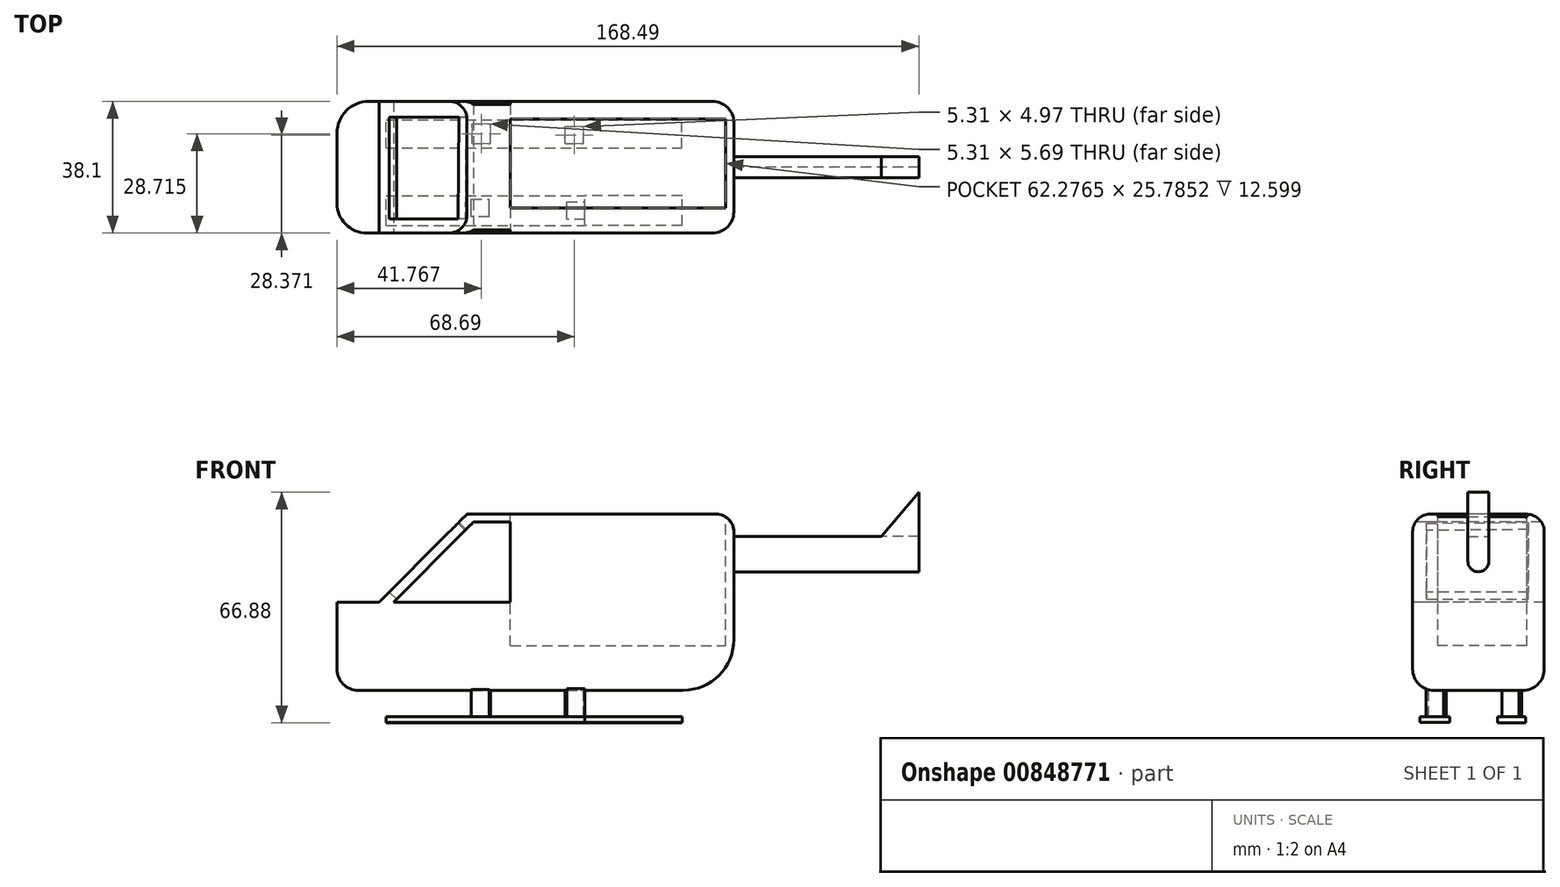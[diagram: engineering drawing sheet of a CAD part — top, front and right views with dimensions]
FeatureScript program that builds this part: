
annotation { "Feature Type Name" : "Feature", "Feature Type Description" : "" }
export const myFeature = defineFeature(function(context is Context, id is Id, definition is map)
    precondition{}
    {
        {
            var Q0;
            Q0=qCreatedBy(makeId("Front.planeOp"),FACE);
            var sketch = newSketch(context, id + "F0", { "sketchPlane" : qUnion([Q0])});
            skLineSegment(sketch, "E0.bottom", {"start": v(-38.01, 25.5) * mm, "end": v(38.01, 25.5) * mm});
            skLineSegment(sketch, "E0.top", {"start": v(-38.01, -25.5) * mm, "end": v(38.01, -25.5) * mm});
            skLineSegment(sketch, "E0.left", {"start": v(-38.01, 25.5) * mm, "end": v(-38.01, -25.5) * mm});
            skLineSegment(sketch, "E0.right", {"start": v(38.01, 25.5) * mm, "end": v(38.01, -25.5) * mm});
            skPoint(sketch, "E0.middle", {"position": v(0, 0) * mm});
            skSolve(sketch);
        }
        {
            var Q0;
            Q0=makeQuery(id+"F0.imprint","IMPRINT",FACE,{"disambiguationData":[TD([[makeQuery(id+"F0.imprint","IMPRINT",EDGE,{"derivedFrom":sQuery(id+"F0.wireOp",EDGE,"E0.bottom")}),-1.0]])]});
            extrude(context, id + "F1", {"entities" : qUnion([Q0]), "depth" : 38.1 * mm, "offsetDistance" : 25.4 * mm});
        }
        {
            var Q0;
            Q0=makeQuery(id+"F1.opExtrude","CAP_FACE",FACE,{"disambiguationData":[OSD([sQuery(id+"F0.wireOp",EDGE,"E0.bottom"),sQuery(id+"F0.wireOp",EDGE,"E0.top"),sQuery(id+"F0.wireOp",EDGE,"E0.left"),sQuery(id+"F0.wireOp",EDGE,"E0.right")])],"isStart":false});
            var sketch = newSketch(context, id + "F2", { "sketchPlane" : qUnion([Q0])});
            skLineSegment(sketch, "E1", {"start": v(-38.01, 0) * mm, "end": v(-12.6, 25.5) * mm});
            skLineSegment(sketch, "E2", {"start": v(-12.6, 25.5) * mm, "end": v(-38.01, 25.5) * mm});
            skLineSegment(sketch, "E3", {"start": v(-38.01, 25.5) * mm, "end": v(-38.01, 0) * mm});
            skSolve(sketch);
        }
        {
            var Q0;
            Q0=makeQuery(id+"F2.imprint","IMPRINT",FACE,{"disambiguationData":[TD([[makeQuery(id+"F2.imprint","IMPRINT",EDGE,{"derivedFrom":sQuery(id+"F2.wireOp",EDGE,"E1")}),1.0]])]});
            extrude(context, id + "F3", {"entities" : qUnion([Q0]), "operationType" : NewBodyOperationType.REMOVE, "oppositeDirection" : true, "depth" : 38.1 * mm, "offsetDistance" : 25.4 * mm});
        }
        {
            var Q0;
            Q0=makeQuery(id+"F1.opExtrude","CAP_FACE",FACE,{"disambiguationData":[OSD([sQuery(id+"F0.wireOp",EDGE,"E0.bottom"),sQuery(id+"F0.wireOp",EDGE,"E0.top"),sQuery(id+"F0.wireOp",EDGE,"E0.left"),sQuery(id+"F0.wireOp",EDGE,"E0.right")])],"isStart":false});
            var sketch = newSketch(context, id + "F4", { "sketchPlane" : qUnion([Q0])});
            skLineSegment(sketch, "E4", {"start": v(-33.84, 0) * mm, "end": v(-10.7, 23.22) * mm});
            skLineSegment(sketch, "E5", {"start": v(-10.7, 23.22) * mm, "end": v(0, 23.22) * mm});
            skLineSegment(sketch, "E6", {"start": v(0, 23.22) * mm, "end": v(0, 0) * mm});
            skLineSegment(sketch, "E7", {"start": v(0, 0) * mm, "end": v(-33.84, 0) * mm});
            skSolve(sketch);
        }
        {
            var Q0;
            Q0=makeQuery(id+"F4.imprint","IMPRINT",FACE,{"disambiguationData":[TD([[makeQuery(id+"F4.imprint","IMPRINT",EDGE,{"derivedFrom":sQuery(id+"F4.wireOp",EDGE,"E4")}),-1.0]])]});
            extrude(context, id + "F5", {"entities" : qUnion([Q0]), "operationType" : NewBodyOperationType.REMOVE, "oppositeDirection" : true, "depth" : 38.1 * mm, "offsetDistance" : 25.4 * mm});
        }
        {
            var Q0;
            Q0=makeQuery(id+"F3.boolean.opBoolean","COPY",FACE,{"derivedFrom":makeQuery(id+"F3.opExtrude","SWEPT_FACE",FACE,{"disambiguationData":[OSD([sQuery(id+"F2.wireOp",EDGE,"E1")])]})});
            var sketch = newSketch(context, id + "F6", { "sketchPlane" : qUnion([Q0])});
            skLineSegment(sketch, "E8", {"start": v(4.6, 5.84) * mm, "end": v(4.6, -22.68) * mm});
            skLineSegment(sketch, "E9", {"start": v(4.6, -22.68) * mm, "end": v(34.03, -22.68) * mm});
            skLineSegment(sketch, "E10", {"start": v(34.03, -22.68) * mm, "end": v(34.03, 5.47) * mm});
            skLineSegment(sketch, "E11", {"start": v(34.03, 5.47) * mm, "end": v(4.6, 5.84) * mm});
            skSolve(sketch);
        }
        {
            var Q0;
            Q0=makeQuery(id+"F6.imprint","IMPRINT",FACE,{"disambiguationData":[TD([[makeQuery(id+"F6.imprint","IMPRINT",EDGE,{"derivedFrom":sQuery(id+"F6.wireOp",EDGE,"E8")}),1.0]])]});
            extrude(context, id + "F7", {"entities" : qUnion([Q0]), "operationType" : NewBodyOperationType.REMOVE, "oppositeDirection" : true, "depth" : 3.8 * mm, "offsetDistance" : 25.4 * mm});
        }
        {
            var Q0;
            Q0=makeQuery(id+"F1.opExtrude","SWEPT_FACE",FACE,{"disambiguationData":[OSD([sQuery(id+"F0.wireOp",EDGE,"E0.right")])]});
            var sketch = newSketch(context, id + "F8", { "sketchPlane" : qUnion([Q0])});
            skLineSegment(sketch, "E12.bottom", {"start": v(-22.1, 19.05) * mm, "end": v(-16.02, 19.05) * mm});
            skLineSegment(sketch, "E12.top", {"start": v(-22.1, 8.82) * mm, "end": v(-16.02, 8.82) * mm});
            skLineSegment(sketch, "E12.left", {"start": v(-22.1, 19.05) * mm, "end": v(-22.1, 8.82) * mm});
            skLineSegment(sketch, "E12.right", {"start": v(-16.02, 19.05) * mm, "end": v(-16.02, 8.82) * mm});
            skSolve(sketch);
        }
        {
            var Q0;
            Q0=makeQuery(id+"F1.opExtrude","SWEPT_FACE",FACE,{"disambiguationData":[OSD([sQuery(id+"F0.wireOp",EDGE,"E0.bottom")])]});
            var sketch = newSketch(context, id + "F9", { "sketchPlane" : qUnion([Q0])});
            skSolve(sketch);
        }
        {
            var Q0;
            Q0=makeQuery(id+"F8.imprint","IMPRINT",FACE,{"disambiguationData":[TD([[makeQuery(id+"F8.imprint","IMPRINT",EDGE,{"derivedFrom":sQuery(id+"F8.wireOp",EDGE,"E12.bottom")}),1.0]])]});
            extrude(context, id + "F10", {"entities" : qUnion([Q0]), "operationType" : NewBodyOperationType.ADD, "depth" : 26.67 * mm, "offsetDistance" : 25.4 * mm});
        }
        {
            var Q0;
            Q0 = qSketchRegion(id + "F8", true);
            extrude(context, id + "F11", {"entities" : qUnion([Q0]), "operationType" : NewBodyOperationType.ADD, "depth" : 80.26 * mm, "offsetDistance" : 25.4 * mm});
        }
        {
            var Q0;
            Q0=makeQuery(id+"F11.opExtrude","SWEPT_FACE",FACE,{"disambiguationData":[OSD([sQuery(id+"F8.wireOp",EDGE,"E12.left")])]});
            var sketch = newSketch(context, id + "F12", { "sketchPlane" : qUnion([Q0])});
            skLineSegment(sketch, "E13", {"start": v(118.28, 19.05) * mm, "end": v(118.28, 31.95) * mm});
            skLineSegment(sketch, "E14", {"start": v(118.28, 31.95) * mm, "end": v(107.4, 19.05) * mm});
            skLineSegment(sketch, "E15", {"start": v(107.4, 19.05) * mm, "end": v(118.28, 19.05) * mm});
            skSolve(sketch);
        }
        {
            var Q0;
            Q0=makeQuery(id+"F12.imprint","IMPRINT",FACE,{"disambiguationData":[TD([[makeQuery(id+"F12.imprint","IMPRINT",EDGE,{"derivedFrom":sQuery(id+"F12.wireOp",EDGE,"E13")}),1.0]])]});
            extrude(context, id + "F13", {"entities" : qUnion([Q0]), "operationType" : NewBodyOperationType.ADD, "oppositeDirection" : true, "depth" : 6.1 * mm, "offsetDistance" : 25.4 * mm});
        }
        {
            var Q0;
            {var subQ0=sQuery(id+"F0.wireOp",EDGE,"E0.bottom");Q0=makeQuery(id+"F9.imprint","IMPRINT",FACE,{"disambiguationData":[TD([[makeQuery(id+"F9.imprint","IMPRINT",EDGE,{"derivedFrom":makeQuery(id+"F1.opExtrude","CAP_EDGE",EDGE,{"disambiguationData":[OSD([subQ0])],"isStart":true})}),-1.0]])]});}
            var sketch = newSketch(context, id + "F14", { "sketchPlane" : qUnion([Q0])});
            skLineSegment(sketch, "E16.bottom", {"start": v(0, -5.02) * mm, "end": v(62.28, -5.02) * mm});
            skLineSegment(sketch, "E16.top", {"start": v(0, -30.8) * mm, "end": v(62.28, -30.8) * mm});
            skLineSegment(sketch, "E16.left", {"start": v(0, -5.02) * mm, "end": v(0, -30.8) * mm});
            skLineSegment(sketch, "E16.right", {"start": v(62.28, -5.02) * mm, "end": v(62.28, -30.8) * mm});
            skSolve(sketch);
        }
        {
            var Q0;
            {var subQ0=sQuery(id+"F14.wireOp",EDGE,"E16.left");Q0=makeQuery(id+"F14.imprint","IMPRINT",FACE,{"disambiguationData":[TD([[makeQuery(id+"F14.imprint","IMPRINT",EDGE,{"derivedFrom":subQ0}),1.0]])]});}
            var Q1;
            {var subQ0=sQuery(id+"F14.wireOp",EDGE,"E16.right");Q1=makeQuery(id+"F14.imprint","IMPRINT",FACE,{"disambiguationData":[TD([[makeQuery(id+"F14.imprint","IMPRINT",EDGE,{"derivedFrom":subQ0}),-1.0]])]});}
            extrude(context, id + "F15", {"entities" : qUnion([Q0, Q1]), "operationType" : NewBodyOperationType.REMOVE, "oppositeDirection" : true, "depth" : 38.1 * mm, "offsetDistance" : 25.4 * mm});
        }
        {
            var Q0;
            Q0=makeQuery(id+"F1.opExtrude","SWEPT_FACE",FACE,{"disambiguationData":[OSD([sQuery(id+"F0.wireOp",EDGE,"E0.left")])]});
            extrude(context, id + "F16", {"entities" : qUnion([Q0]), "operationType" : NewBodyOperationType.ADD, "depth" : 12.2 * mm, "offsetDistance" : 25.4 * mm});
        }
        {
            var Q0;
            {var subQ0=sQuery(id+"F0.wireOp",EDGE,"E0.top");Q0=makeQuery(id+"F16.boolean.opBoolean","MERGE",FACE,{"derivedFrom":[makeQuery(id+"F10.boolean.opBoolean","MERGE",FACE,{"derivedFrom":[makeQuery(id+"F1.opExtrude","SWEPT_FACE",FACE,{"disambiguationData":[OSD([subQ0])]}),makeQuery(id+"F10.opExtrude","SWEPT_FACE",FACE,{"disambiguationData":[OSD([subQ0,sQuery(id+"F0.wireOp",EDGE,"E0.right")])]})]}),makeQuery(id+"F16.opExtrude","SWEPT_FACE",FACE,{"disambiguationData":[OSD([subQ0,sQuery(id+"F0.wireOp",EDGE,"E0.left")])]})]});}
            var sketch = newSketch(context, id + "F17", { "sketchPlane" : qUnion([Q0])});
            skLineSegment(sketch, "E17.bottom", {"start": v(-11.29, 33.46) * mm, "end": v(-6.17, 33.46) * mm});
            skLineSegment(sketch, "E17.top", {"start": v(-11.29, 28.34) * mm, "end": v(-6.17, 28.34) * mm});
            skLineSegment(sketch, "E17.left", {"start": v(-11.29, 33.46) * mm, "end": v(-11.29, 28.34) * mm});
            skLineSegment(sketch, "E17.right", {"start": v(-6.17, 33.46) * mm, "end": v(-6.17, 28.34) * mm});
            skSolve(sketch);
        }
        {
            var Q0;
            Q0=makeQuery(id+"F17.imprint","IMPRINT",FACE,{"disambiguationData":[TD([[makeQuery(id+"F17.imprint","IMPRINT",EDGE,{"derivedFrom":sQuery(id+"F17.wireOp",EDGE,"E17.bottom")}),1.0]])]});
            var sketch = newSketch(context, id + "F18", { "sketchPlane" : qUnion([Q0])});
            skLineSegment(sketch, "E18.bottom", {"start": v(-11.1, 12.23) * mm, "end": v(-5.79, 12.23) * mm});
            skLineSegment(sketch, "E18.top", {"start": v(-11.1, 6.54) * mm, "end": v(-5.79, 6.54) * mm});
            skLineSegment(sketch, "E18.left", {"start": v(-11.1, 12.23) * mm, "end": v(-11.1, 6.54) * mm});
            skLineSegment(sketch, "E18.right", {"start": v(-5.79, 12.23) * mm, "end": v(-5.79, 6.54) * mm});
            skSolve(sketch);
        }
        {
            var Q0;
            Q0=makeQuery(id+"F17.imprint","IMPRINT",FACE,{"disambiguationData":[TD([[makeQuery(id+"F17.imprint","IMPRINT",EDGE,{"derivedFrom":sQuery(id+"F17.wireOp",EDGE,"E17.bottom")}),1.0]])]});
            var sketch = newSketch(context, id + "F19", { "sketchPlane" : qUnion([Q0])});
            skLineSegment(sketch, "E19.bottom", {"start": v(16.4, 34.22) * mm, "end": v(21.51, 34.22) * mm});
            skLineSegment(sketch, "E19.top", {"start": v(16.4, 29.1) * mm, "end": v(21.51, 29.1) * mm});
            skLineSegment(sketch, "E19.left", {"start": v(16.4, 34.22) * mm, "end": v(16.4, 29.1) * mm});
            skLineSegment(sketch, "E19.right", {"start": v(21.51, 34.22) * mm, "end": v(21.51, 29.1) * mm});
            skSolve(sketch);
        }
        {
            var Q0;
            Q0=makeQuery(id+"F17.imprint","IMPRINT",FACE,{"disambiguationData":[TD([[makeQuery(id+"F17.imprint","IMPRINT",EDGE,{"derivedFrom":sQuery(id+"F17.wireOp",EDGE,"E17.bottom")}),1.0]])]});
            var sketch = newSketch(context, id + "F20", { "sketchPlane" : qUnion([Q0])});
            skLineSegment(sketch, "E20.bottom", {"start": v(15.83, 12.21) * mm, "end": v(21.13, 12.21) * mm});
            skLineSegment(sketch, "E20.top", {"start": v(15.83, 7.24) * mm, "end": v(21.13, 7.24) * mm});
            skLineSegment(sketch, "E20.left", {"start": v(15.83, 12.21) * mm, "end": v(15.83, 7.24) * mm});
            skLineSegment(sketch, "E20.right", {"start": v(21.13, 12.21) * mm, "end": v(21.13, 7.24) * mm});
            skSolve(sketch);
        }
        {
            var Q0;
            Q0=makeQuery(id+"F18.imprint","IMPRINT",FACE,{"disambiguationData":[TD([[makeQuery(id+"F18.imprint","IMPRINT",EDGE,{"derivedFrom":sQuery(id+"F18.wireOp",EDGE,"E18.bottom")}),-1.0]])]});
            extrude(context, id + "F21", {"entities" : qUnion([Q0]), "operationType" : NewBodyOperationType.ADD, "depth" : 7.62 * mm, "offsetDistance" : 25.4 * mm});
        }
        {
            var Q0;
            Q0=makeQuery(id+"F17.imprint","IMPRINT",FACE,{"disambiguationData":[TD([[makeQuery(id+"F17.imprint","IMPRINT",EDGE,{"derivedFrom":sQuery(id+"F17.wireOp",EDGE,"E17.bottom")}),-1.0]])]});
            extrude(context, id + "F22", {"entities" : qUnion([Q0]), "operationType" : NewBodyOperationType.ADD, "depth" : 7.62 * mm, "offsetDistance" : 25.4 * mm});
        }
        {
            var Q0;
            Q0=makeQuery(id+"F19.imprint","IMPRINT",FACE,{"disambiguationData":[TD([[makeQuery(id+"F19.imprint","IMPRINT",EDGE,{"derivedFrom":sQuery(id+"F19.wireOp",EDGE,"E19.bottom")}),-1.0]])]});
            extrude(context, id + "F23", {"entities" : qUnion([Q0]), "operationType" : NewBodyOperationType.ADD, "depth" : 7.62 * mm, "offsetDistance" : 25.4 * mm});
        }
        {
            var Q0;
            Q0=makeQuery(id+"F20.imprint","IMPRINT",FACE,{"disambiguationData":[TD([[makeQuery(id+"F20.imprint","IMPRINT",EDGE,{"derivedFrom":sQuery(id+"F20.wireOp",EDGE,"E20.bottom")}),-1.0]])]});
            extrude(context, id + "F24", {"entities" : qUnion([Q0]), "operationType" : NewBodyOperationType.ADD, "depth" : 7.62 * mm, "offsetDistance" : 25.4 * mm});
        }
        {
            var Q0;
            Q0=makeQuery(id+"F24.opExtrude","SWEPT_FACE",FACE,{"disambiguationData":[OSD([sQuery(id+"F20.wireOp",EDGE,"E20.right")])]});
            var sketch = newSketch(context, id + "F25", { "sketchPlane" : qUnion([Q0])});
            skLineSegment(sketch, "E21.bottom", {"start": v(-13.52, -33.12) * mm, "end": v(-5.4, -33.12) * mm});
            skLineSegment(sketch, "E21.top", {"start": v(-13.52, -34.93) * mm, "end": v(-5.4, -34.93) * mm});
            skLineSegment(sketch, "E21.left", {"start": v(-13.52, -33.12) * mm, "end": v(-13.52, -34.93) * mm});
            skLineSegment(sketch, "E21.right", {"start": v(-5.4, -33.12) * mm, "end": v(-5.4, -34.93) * mm});
            skSolve(sketch);
        }
        {
            var Q0;
            Q0=makeQuery(id+"F25.imprint","IMPRINT",FACE,{"disambiguationData":[TD([[makeQuery(id+"F25.imprint","IMPRINT",EDGE,{"derivedFrom":sQuery(id+"F25.wireOp",EDGE,"E21.top")}),1.0]])]});
            extrude(context, id + "F26", {"entities" : qUnion([Q0]), "operationType" : NewBodyOperationType.ADD, "oppositeDirection" : true, "depth" : 57.15 * mm, "offsetDistance" : 25.4 * mm});
        }
        {
            var Q0;
            Q0=makeQuery(id+"F26.boolean.opBoolean","MERGE",FACE,{"derivedFrom":[makeQuery(id+"F24.opExtrude","SWEPT_FACE",FACE,{"disambiguationData":[OSD([sQuery(id+"F20.wireOp",EDGE,"E20.right")])]}),makeQuery(id+"F26.opExtrude","CAP_FACE",FACE,{"disambiguationData":[OSD([sQuery(id+"F25.wireOp",EDGE,"E21.bottom"),sQuery(id+"F25.wireOp",EDGE,"E21.top"),sQuery(id+"F25.wireOp",EDGE,"E21.left"),sQuery(id+"F25.wireOp",EDGE,"E21.right")])],"isStart":true})]});
            var sketch = newSketch(context, id + "F27", { "sketchPlane" : qUnion([Q0])});
            skLineSegment(sketch, "E22.bottom", {"start": v(-13.52, -34.93) * mm, "end": v(-5.4, -34.93) * mm});
            skLineSegment(sketch, "E22.top", {"start": v(-13.52, -33.12) * mm, "end": v(-5.4, -33.12) * mm});
            skLineSegment(sketch, "E22.left", {"start": v(-13.52, -34.93) * mm, "end": v(-13.52, -33.12) * mm});
            skLineSegment(sketch, "E22.right", {"start": v(-5.4, -34.93) * mm, "end": v(-5.4, -33.12) * mm});
            skSolve(sketch);
        }
        {
            var Q0;
            Q0=makeQuery(id+"F27.imprint","IMPRINT",FACE,{"disambiguationData":[TD([[makeQuery(id+"F27.imprint","IMPRINT",EDGE,{"derivedFrom":sQuery(id+"F27.wireOp",EDGE,"E22.bottom")}),1.0]])]});
            extrude(context, id + "F28", {"entities" : qUnion([Q0]), "operationType" : NewBodyOperationType.ADD, "depth" : 28.45 * mm, "offsetDistance" : 25.4 * mm});
        }
        {
            var Q0;
            Q0=makeQuery(id+"F23.opExtrude","SWEPT_FACE",FACE,{"disambiguationData":[OSD([sQuery(id+"F19.wireOp",EDGE,"E19.right")])]});
            var sketch = newSketch(context, id + "F29", { "sketchPlane" : qUnion([Q0])});
            skLineSegment(sketch, "E23.bottom", {"start": v(-35.94, -33.12) * mm, "end": v(-27.31, -33.12) * mm});
            skLineSegment(sketch, "E23.top", {"start": v(-35.94, -34.77) * mm, "end": v(-27.31, -34.77) * mm});
            skLineSegment(sketch, "E23.left", {"start": v(-35.94, -33.12) * mm, "end": v(-35.94, -34.77) * mm});
            skLineSegment(sketch, "E23.right", {"start": v(-27.31, -33.12) * mm, "end": v(-27.31, -34.77) * mm});
            skSolve(sketch);
        }
        {
            var Q0;
            Q0=makeQuery(id+"F29.imprint","IMPRINT",FACE,{"disambiguationData":[TD([[makeQuery(id+"F29.imprint","IMPRINT",EDGE,{"derivedFrom":sQuery(id+"F29.wireOp",EDGE,"E23.top")}),1.0]])]});
            extrude(context, id + "F30", {"entities" : qUnion([Q0]), "depth" : 28.17 * mm, "offsetDistance" : 25.4 * mm});
        }
        {
            var Q0;
            Q0=makeQuery(id+"F30.opExtrude","CAP_FACE",FACE,{"disambiguationData":[OSD([sQuery(id+"F29.wireOp",EDGE,"E23.bottom"),sQuery(id+"F29.wireOp",EDGE,"E23.top"),sQuery(id+"F29.wireOp",EDGE,"E23.left"),sQuery(id+"F29.wireOp",EDGE,"E23.right")])],"isStart":true});
            extrude(context, id + "F31", {"entities" : qUnion([Q0]), "depth" : 57.5 * mm, "offsetDistance" : 25.4 * mm});
        }
        {
            var Q0;
            {var subQ0=sQuery(id+"F0.wireOp",EDGE,"E0.left");Q0=makeQuery(id+"F16.opExtrude","CAP_EDGE",EDGE,{"disambiguationData":[OSD([subQ0]),TDD([makeQuery(id+"F1.opExtrude","CAP_EDGE",EDGE,{"disambiguationData":[OSD([subQ0])],"isStart":false})])],"isStart":false});}
            fillet(context, id + "F32", {"entities" : qUnion([Q0]), "radius" : 8.58 * mm, "tangentPropagation" : true, "allowEdgeOverflow" : false});
        }
        {
            var Q0;
            {var subQ0=sQuery(id+"F0.wireOp",EDGE,"E0.left");Q0=makeQuery(id+"F16.opExtrude","CAP_EDGE",EDGE,{"disambiguationData":[OSD([subQ0]),TDD([makeQuery(id+"F1.opExtrude","CAP_EDGE",EDGE,{"disambiguationData":[OSD([subQ0])],"isStart":true})])],"isStart":false});}
            fillet(context, id + "F33", {"entities" : qUnion([Q0]), "radius" : 9.2 * mm, "tangentPropagation" : true, "allowEdgeOverflow" : false});
        }
        {
            var Q0;
            Q0=makeQuery(id+"F10.opExtrude","CAP_EDGE",EDGE,{"disambiguationData":[OSD([sQuery(id+"F0.wireOp",EDGE,"E0.top"),sQuery(id+"F0.wireOp",EDGE,"E0.right")])],"isStart":false});
            fillet(context, id + "F34", {"entities" : qUnion([Q0]), "radius" : 14.72 * mm, "tangentPropagation" : true, "allowEdgeOverflow" : false});
        }
        {
            var Q0;
            {var subQ0=sQuery(id+"F0.wireOp",EDGE,"E0.right");Q0=makeQuery(id+"F10.opExtrude","CAP_EDGE",EDGE,{"disambiguationData":[OSD([subQ0]),TDD([makeQuery(id+"F8.imprint","IMPRINT",EDGE,{"derivedFrom":makeQuery(id+"F1.opExtrude","CAP_EDGE",EDGE,{"disambiguationData":[OSD([subQ0])],"isStart":false})})])],"isStart":false});}
            fillet(context, id + "F35", {"entities" : qUnion([Q0]), "radius" : 6.13 * mm, "tangentPropagation" : true, "allowEdgeOverflow" : false});
        }
        {
            var Q0;
            {var subQ0=sQuery(id+"F0.wireOp",EDGE,"E0.right");var subQ1=sQuery(id+"F0.wireOp",EDGE,"E0.bottom");Q0=makeQuery(id+"F10.boolean.opBoolean","MERGE",EDGE,{"derivedFrom":[makeQuery(id+"F1.opExtrude","CAP_EDGE",EDGE,{"disambiguationData":[OSD([subQ1])],"isStart":true}),makeQuery(id+"F10.opExtrude","SWEPT_EDGE",EDGE,{"disambiguationData":[OSD([subQ1,subQ0]),TDD([makeQuery(id+"F8.imprint","INTERSECT",VERTEX,{"derivedFrom":[makeQuery(id+"F1.opExtrude","SWEPT_EDGE",EDGE,{"disambiguationData":[OSD([subQ1,subQ0])]}),makeQuery(id+"F1.opExtrude","CAP_EDGE",EDGE,{"disambiguationData":[OSD([subQ0])],"isStart":true})]})])]})]});}
            fillet(context, id + "F36", {"entities" : qUnion([Q0]), "radius" : 5.08 * mm, "tangentPropagation" : true, "allowEdgeOverflow" : false});
        }
        {
            var Q0;
            Q0=makeQuery(id+"F11.opExtrude","SWEPT_EDGE",EDGE,{"disambiguationData":[OSD([sQuery(id+"F8.wireOp",EDGE,"E12.top"),sQuery(id+"F8.wireOp",EDGE,"E12.left")])]});
            fillet(context, id + "F37", {"entities" : qUnion([Q0]), "radius" : 3.07 * mm, "tangentPropagation" : true, "allowEdgeOverflow" : false});
        }
        {
            var Q0;
            Q0=makeQuery(id+"F11.opExtrude","SWEPT_EDGE",EDGE,{"disambiguationData":[OSD([sQuery(id+"F8.wireOp",EDGE,"E12.top"),sQuery(id+"F8.wireOp",EDGE,"E12.right")])]});
            fillet(context, id + "F38", {"entities" : qUnion([Q0]), "radius" : 3.07 * mm, "tangentPropagation" : true, "allowEdgeOverflow" : false});
        }
    });
